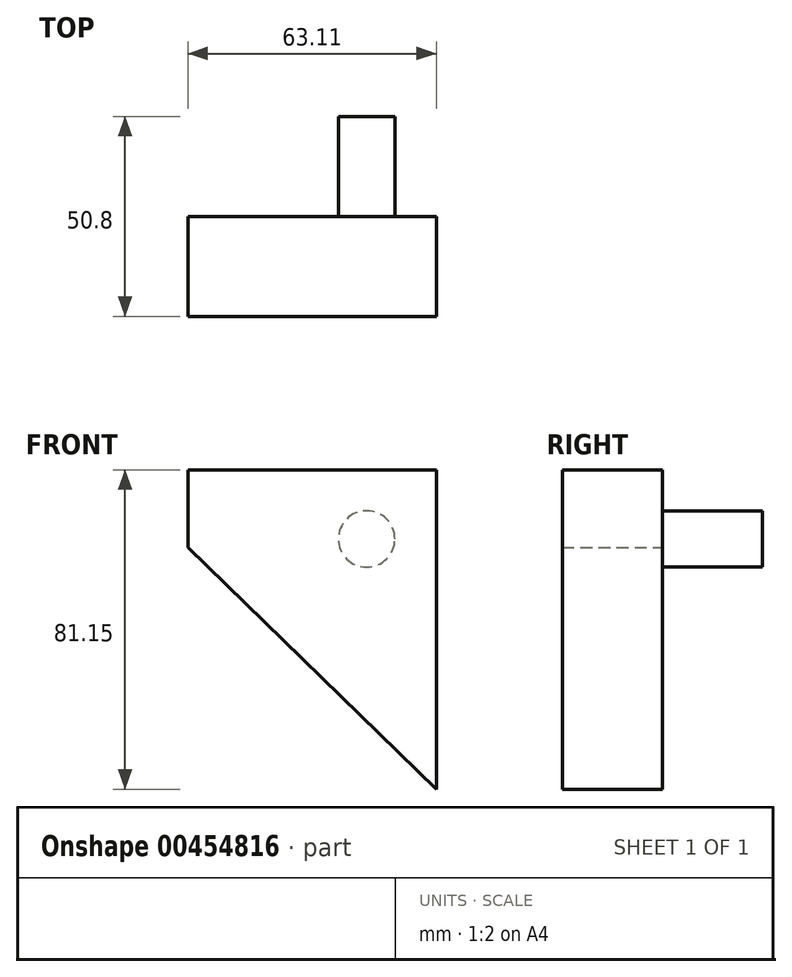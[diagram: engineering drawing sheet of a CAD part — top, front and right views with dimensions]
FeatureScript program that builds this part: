
annotation { "Feature Type Name" : "Feature", "Feature Type Description" : "" }
export const myFeature = defineFeature(function(context is Context, id is Id, definition is map)
    precondition{}
    {
        {
            var Q0;
            Q0=qCreatedBy(makeId("Front.planeOp"),FACE);
            var sketch = newSketch(context, id + "F0", { "sketchPlane" : qUnion([Q0])});
            skPoint(sketch, "E0.0", {"position": v(0, 0) * mm});
            skLineSegment(sketch, "E1", {"start": v(-32.8, 35.46) * mm, "end": v(-32.8, 55.17) * mm});
            skLineSegment(sketch, "E2", {"start": v(-32.8, 55.17) * mm, "end": v(30.31, 55.17) * mm});
            skLineSegment(sketch, "E3", {"start": v(30.31, 55.17) * mm, "end": v(30.31, -25.98) * mm});
            skLineSegment(sketch, "E4", {"start": v(30.31, -25.98) * mm, "end": v(-32.8, 35.46) * mm});
            skSolve(sketch);
        }
        {
            var Q0;
            Q0 = qSketchRegion(id + "F0", true);
            extrude(context, id + "F1", {"entities" : qUnion([Q0]), "depth" : 25.4 * mm});
        }
        {
            var Q0;
            Q0=makeQuery(id+"F1.opExtrude","CAP_FACE",FACE,{"disambiguationData":[OSD([sQuery(id+"F0.wireOp",EDGE,"E1"),sQuery(id+"F0.wireOp",EDGE,"E2"),sQuery(id+"F0.wireOp",EDGE,"E3"),sQuery(id+"F0.wireOp",EDGE,"E4")])],"isStart":false});
            var sketch = newSketch(context, id + "F2", { "sketchPlane" : qUnion([Q0])});
            skCircle(sketch, "E5", {"center": v(12.6, 37.6) * mm, "radius": 7.17 * mm});
            skSolve(sketch);
        }
        {
            var Q0;
            Q0 = qSketchRegion(id + "F2", true);
            extrude(context, id + "F3", {"entities" : qUnion([Q0]), "operationType" : NewBodyOperationType.ADD, "oppositeDirection" : true, "depth" : 50.8 * mm});
        }
    });
